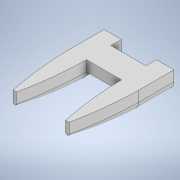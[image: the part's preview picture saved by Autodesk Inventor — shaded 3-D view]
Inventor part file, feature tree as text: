
AUTODESK INVENTOR PART (.ipt)
format: ipt  version: 2020.3 (Build 243373000, 373)  size: 291,328 bytes
history: native  units: mm
features: plane x6, sketch x4, extrude x2, loft x1, chamfer x1, mirror x1, other x1, projected_geometry x1
ambient origin geometry x8: Origin, YZ Plane, XZ Plane, XY Plane, X Axis, Y Axis, Z Axis, Center Point
bodies: Solid1 (feature_tree)
feature tree (17):
  sketch  "Sketch1"  dims[d0=100.0mm d1=240.0mm]
  plane  "Work Plane1"
  plane  "Work Plane2"
  plane  "Work Plane3"
  plane  "Work Plane4"
  extrude  "Extrusion1"  Depth=240.0mm
  loft  "Loft3"
  chamfer  "Chamfer1"  Distance=18.0mm
  plane  "Work Plane7"
  mirror  "Mirror1"
  extrude  "Extrusion2"  Depth=25.0mm
  sketch  "Sketch3"  dims[d2=280.0mm d3=30.0mm]
  sketch  "Sketch4"  dims[d4=50.0mm]
  other  "Edges3"
  plane  "Work Plane5"
  sketch  "Sketch5"  dims[d5=30.0mm d7=18.0mm d8=25.0mm d9=18.0mm d10=25.0mm d11=10.0mm d12=0.0mm d13=25.0mm d14=13.217565mm d16=7.930539mm d17=12.5mm d18=12.5mm d19=7.930539mm d24=10.0mm d25=5.0mm d26=3.0mm d27=3.0mm d28=5.0mm d29=5.0mm d35=0.0mm d36=90.0deg d37=0.0mm d38=90.0deg d39=0.0mm d40=90.0deg d42=2.0mm d43=2.0mm d44=45.0deg d46=-100.0mm d47=30.0mm d48=10.0mm d49=0.0mm]
  projected_geometry  "Projected Loop2"
